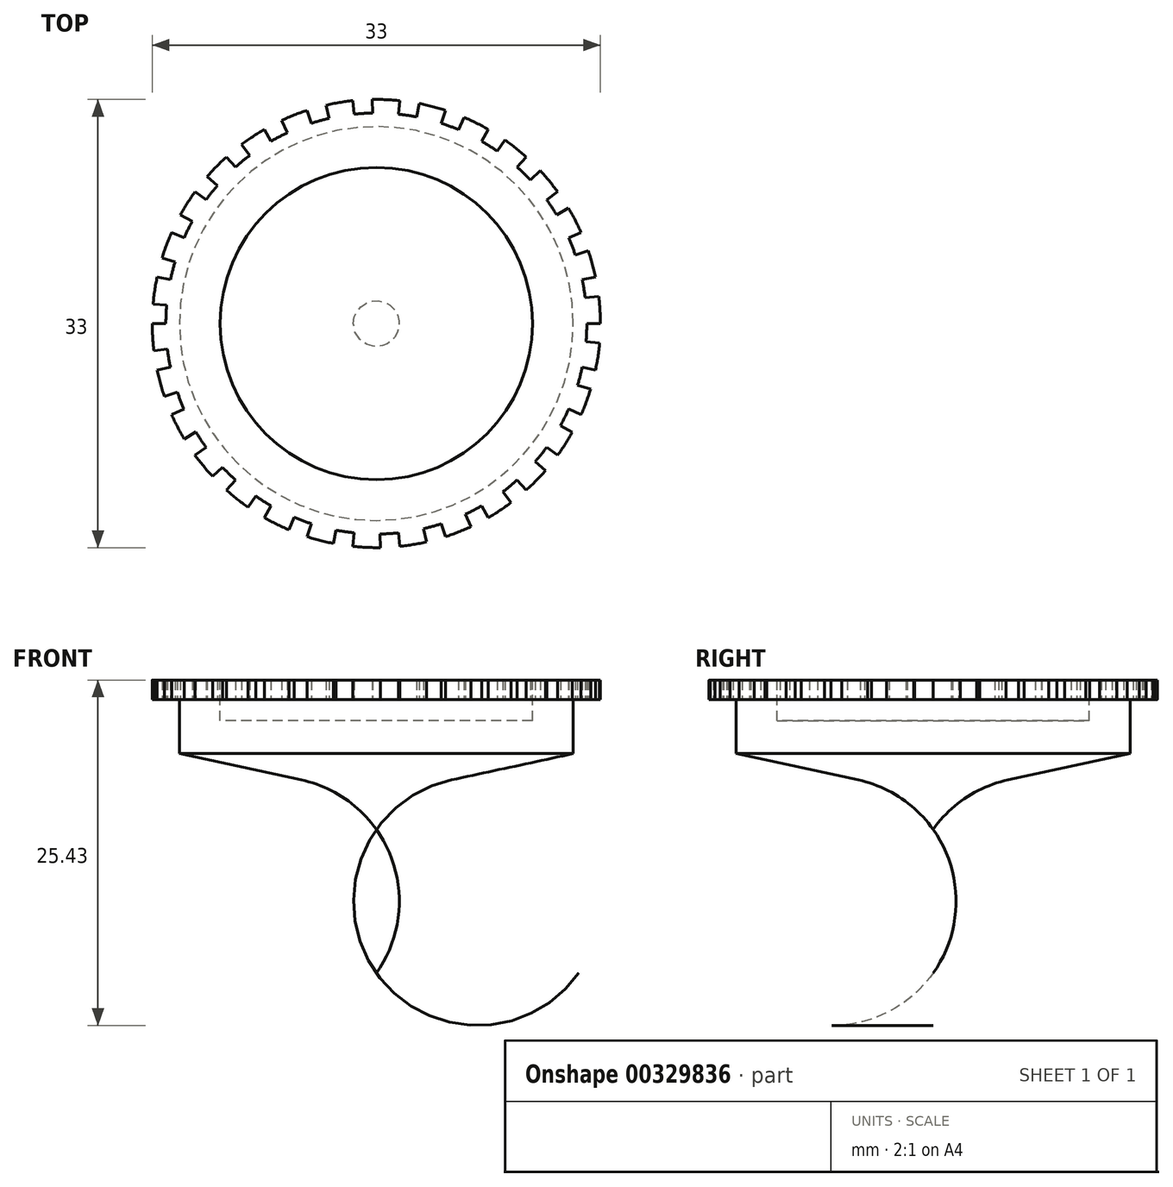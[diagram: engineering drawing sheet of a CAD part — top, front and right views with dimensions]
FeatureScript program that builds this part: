
annotation { "Feature Type Name" : "Feature", "Feature Type Description" : "" }
export const myFeature = defineFeature(function(context is Context, id is Id, definition is map)
    precondition{}
    {
        {
            var Q0;
            Q0=qCreatedBy(makeId("Front.planeOp"),FACE);
            var sketch = newSketch(context, id + "F0", { "sketchPlane" : qUnion([Q0])});
            skLineSegment(sketch, "E0", {"start": v(11.5, 11) * mm, "end": v(14.5, 11) * mm});
            skLineSegment(sketch, "E1", {"start": v(14.5, 11) * mm, "end": v(14.5, 5.58) * mm});
            skLineSegment(sketch, "E2", {"start": v(14.5, 5.58) * mm, "end": v(5.54, 3.65) * mm});
            skArc(sketch, "E3", {"start": v(5.54, 3.65) * mm, "mid": v(2.43, 2.34) * mm, "end": v(0, 0) * mm});
            skLineSegment(sketch, "E4", {"start": v(11.5, 11) * mm, "end": v(11.5, 8) * mm});
            skLineSegment(sketch, "E5", {"start": v(11.5, 8) * mm, "end": v(0, 8) * mm});
            skLineSegment(sketch, "E6", {"start": v(0, 8) * mm, "end": v(0, 0) * mm});
            skLineSegment(sketch, "E7.bottom", {"start": v(14.5, 11) * mm, "end": v(16.5, 11) * mm});
            skLineSegment(sketch, "E7.top", {"start": v(14.5, 9.56) * mm, "end": v(16.5, 9.56) * mm});
            skLineSegment(sketch, "E7.left", {"start": v(14.5, 11) * mm, "end": v(14.5, 9.56) * mm});
            skLineSegment(sketch, "E7.right", {"start": v(16.5, 11) * mm, "end": v(16.5, 9.56) * mm});
            skSolve(sketch);
        }
        {
            var Q0;
            Q0=makeQuery(id+"F0.imprint","IMPRINT",FACE,{"disambiguationData":[TD([[makeQuery(id+"F0.imprint","IMPRINT",EDGE,{"derivedFrom":sQuery(id+"F0.wireOp",EDGE,"E0")}),-1.0]])]});
            var Q1;
            Q1=makeQuery(id+"F0.imprint","IMPRINT",FACE,{"disambiguationData":[TD([[makeQuery(id+"F0.imprint","IMPRINT",EDGE,{"derivedFrom":sQuery(id+"F0.wireOp",EDGE,"E7.bottom")}),-1.0]])]});
            var Q2;
            Q2=sQuery(id+"F0.wireOp",EDGE,"E6");
            revolve(context, id + "F1", {"entities" : qUnion([Q0, Q1]), "axis" : qUnion([Q2]), "revolveType" : RevolveType.FULL});
        }
        {
            var Q0;
            Q0=qCreatedBy(makeId("Front.planeOp"),FACE);
            var sketch = newSketch(context, id + "F2", { "sketchPlane" : qUnion([Q0])});
            skLineSegment(sketch, "E8.bottom", {"start": v(16.5, 11) * mm, "end": v(15.5, 11) * mm});
            skLineSegment(sketch, "E8.top", {"start": v(16.5, 9.56) * mm, "end": v(15.5, 9.56) * mm});
            skLineSegment(sketch, "E8.left", {"start": v(16.5, 11) * mm, "end": v(16.5, 9.56) * mm});
            skLineSegment(sketch, "E8.right", {"start": v(15.5, 11) * mm, "end": v(15.5, 9.56) * mm});
            skSolve(sketch);
        }
        {
            var Q0;
            Q0 = qSketchRegion(id + "F2", true);
            var Q1;
            Q1=sQuery(id+"F0.wireOp",EDGE,"E6");
            revolve(context, id + "F3", {"entities" : qUnion([Q0]), "axis" : qUnion([Q1]), "revolveType" : RevolveType.ONE_DIRECTION, "angle" : 5 * degree});
        }
        {
            var Q0;
            Q0=makeQuery(id+"F3.opRevolve","SWEPT_BODY",BODY,{"disambiguationData":[OSD([sQuery(id+"F2.wireOp",EDGE,"E8.bottom"),sQuery(id+"F2.wireOp",EDGE,"E8.top"),sQuery(id+"F2.wireOp",EDGE,"E8.left"),sQuery(id+"F2.wireOp",EDGE,"E8.right")])]});
            var Q1;
            Q1=sQuery(id+"F0.wireOp",EDGE,"E6");
            circularPattern(context, id + "F4", {"operationType" : NewBodyOperationType.REMOVE, "entities" : qUnion([Q0]), "axis" : qUnion([Q1]), "angle" : 360 * degree, "instanceCount" : 30, "equalSpace" : true});
        }
    });
